# Revit family: RWSC
name_source: partatom
category: Lighting Fixtures
revit_build: Autodesk Revit 2014 (Build: 20130308_1515(x64)
units: mm (PartAtom-declared; Revit-internal decimal feet)

## types (1)
- RWSC
    Apparent Load = 25 VA
    Assembly Code = D5020200
    Color Filter = 16777215
    Connector Description = Lighting Connector
    Default Elevation = 48 "
    Description = The RWSC LED radius wall sconce series offers a combination of light distributions that wash the building facade while the radial soft form housing accentuates building architectural design elements in all commercial and residential applications.
    Dimming Lamp Color Temperature Shift = <None>
    Features = Durable cast aluminum housing
• Integrated design eliminates high angle brightness
• Completely sealed, flat tempered glass lenses, UL listed for use in wet
locations
• DLC, Downlight only, full cut-off
    Housing Material = Paint - Hubbell - Carbon Black
    Lamp = LED
    Length = 48 "
    Load Classification = Lighting
    Manufacturer = Security Lighting
    Model = RWSC
    Photometric Web File = generic
    Power Factor = 1
    Product Doucmentation Link = https://hubbellcdn.com
    Product Page URL = https://www.hubbell.com
    Reflector Finish = Hubbell - White Glass
    Tilt Angle = 60.00°
    URL = https://www.hubbell.com
    Voltage = 120 V
    Warranty = 5 years Warranty
    Wattage Comments = 25
    Watts = 25 W
    Width = 11.63 "
    Width 1 = 5 "

## geometry (parser evidence)
native form markers: Sweep x5
no freeform markers — native parametric forms only
